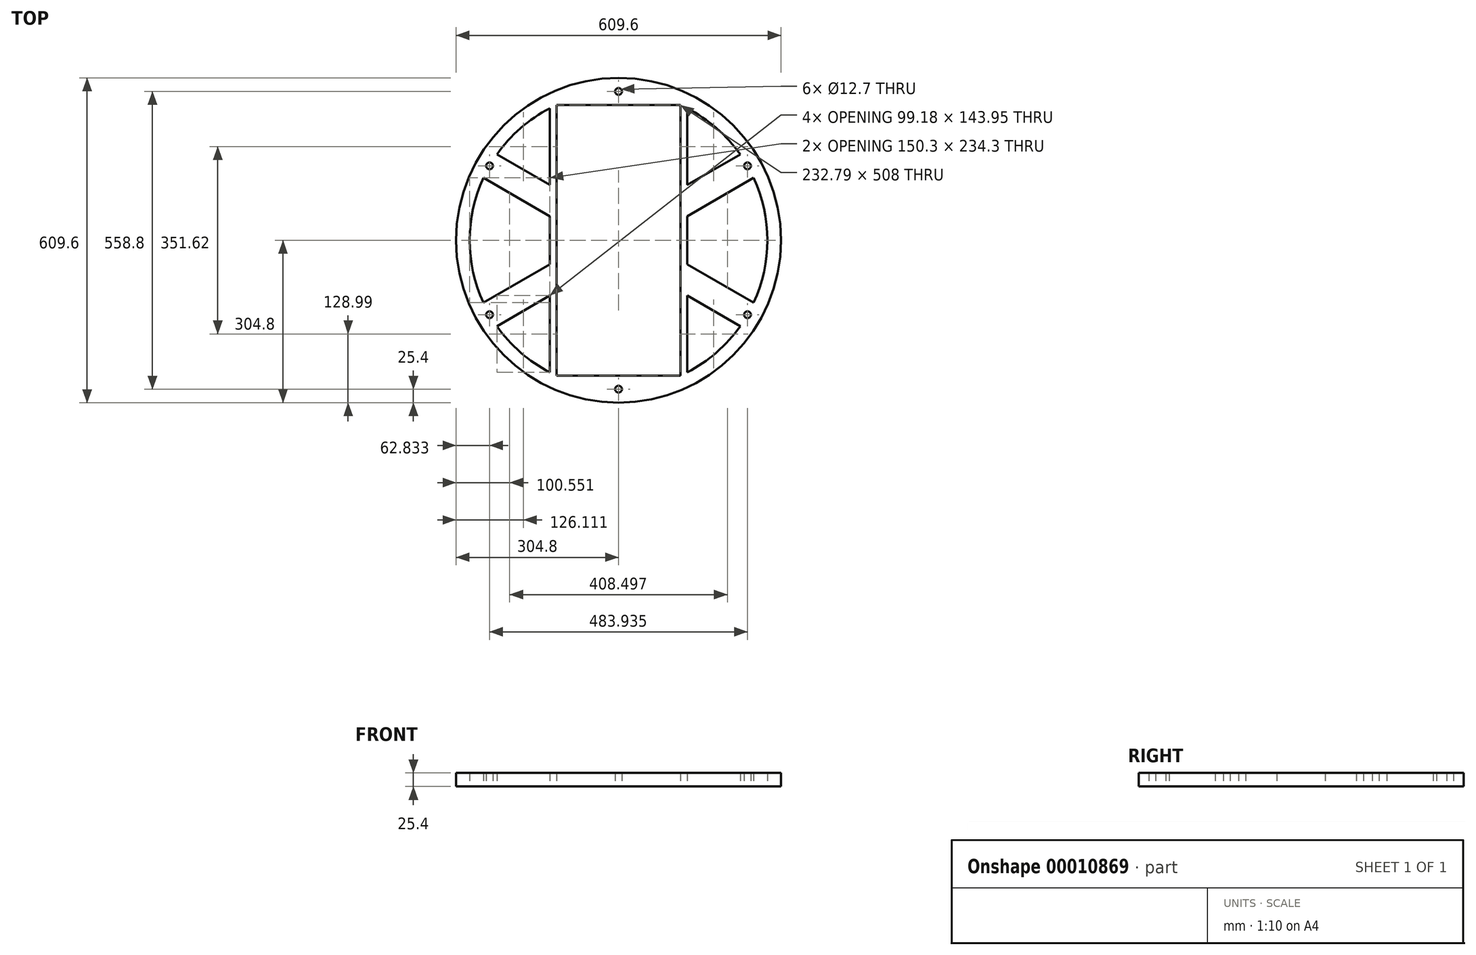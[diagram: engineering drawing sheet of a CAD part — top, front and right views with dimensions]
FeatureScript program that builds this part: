
annotation { "Feature Type Name" : "Feature", "Feature Type Description" : "" }
export const myFeature = defineFeature(function(context is Context, id is Id, definition is map)
    precondition{}
    {
        {
            var Q0;
            Q0=qCreatedBy(makeId("Top.planeOp"),FACE);
            var sketch = newSketch(context, id + "F0", { "sketchPlane" : qUnion([Q0])});
            skCircle(sketch, "E0", {"center": v(0, 0) * mm, "radius": 304.8 * mm});
            skArc(sketch, "E1.0", {"start": v(-129.1, 247.79) * mm, "mid": v(-183.87, 210.37) * mm, "end": v(-228.28, 161.1) * mm});
            skArc(sketch, "E2.1.0", {"start": v(-253.65, 117.15) * mm, "mid": v(-219.97, 127) * mm, "end": v(-228.28, 161.1) * mm});
            skArc(sketch, "E2.2.0", {"start": v(-228.28, -161.1) * mm, "mid": v(-219.97, -127) * mm, "end": v(-253.65, -117.15) * mm});
            skArc(sketch, "E2.4.0", {"start": v(253.65, -117.15) * mm, "mid": v(219.97, -127) * mm, "end": v(228.28, -161.1) * mm});
            skArc(sketch, "E2.5.0", {"start": v(228.28, 161.1) * mm, "mid": v(219.97, 127) * mm, "end": v(253.65, 117.15) * mm});
            skLineSegment(sketch, "E3.bottom", {"start": v(-116.4, 254) * mm, "end": v(116.4, 254) * mm});
            skLineSegment(sketch, "E3.top", {"start": v(-116.4, -254) * mm, "end": v(116.4, -254) * mm});
            skLineSegment(sketch, "E3.left", {"start": v(-116.4, 254) * mm, "end": v(-116.4, -254) * mm});
            skLineSegment(sketch, "E3.right", {"start": v(116.4, 254) * mm, "end": v(116.4, -254) * mm});
            skArc(sketch, "E4.trimOffspring", {"start": v(-253.65, 117.15) * mm, "mid": v(-279.4, 0) * mm, "end": v(-253.65, -117.15) * mm});
            skArc(sketch, "E5.trimOffspring", {"start": v(-228.28, -161.1) * mm, "mid": v(-183.87, -210.37) * mm, "end": v(-129.1, -247.79) * mm});
            skArc(sketch, "E6.trimOffspring", {"start": v(253.65, -117.15) * mm, "mid": v(279.4, 0) * mm, "end": v(253.65, 117.15) * mm});
            skArc(sketch, "E7.trimOffspring", {"start": v(228.28, 161.1) * mm, "mid": v(183.87, 210.37) * mm, "end": v(129.1, 247.79) * mm});
            skLineSegment(sketch, "E8.0", {"start": v(-129.1, 247.79) * mm, "end": v(-129.1, 103.83) * mm});
            skLineSegment(sketch, "E8.2", {"start": v(129.1, 247.79) * mm, "end": v(129.1, 103.83) * mm});
            skPoint(sketch, "E9.center.orphan", {"position": v(0, 279.4) * mm});
            skArc(sketch, "E10.trimOffspring", {"start": v(129.1, -247.79) * mm, "mid": v(183.87, -210.37) * mm, "end": v(228.28, -161.1) * mm});
            skLineSegment(sketch, "E11", {"start": v(-253.65, 117.15) * mm, "end": v(-129.1, 45.24) * mm});
            skLineSegment(sketch, "E12", {"start": v(-228.28, 161.1) * mm, "end": v(-129.1, 103.83) * mm});
            skLineSegment(sketch, "E13", {"start": v(-253.65, -117.15) * mm, "end": v(-129.1, -45.24) * mm});
            skLineSegment(sketch, "E14", {"start": v(253.65, 117.15) * mm, "end": v(129.1, 45.24) * mm});
            skLineSegment(sketch, "E15.trimOffspring", {"start": v(129.1, -103.83) * mm, "end": v(228.28, -161.1) * mm});
            skLineSegment(sketch, "E16.trimOffspring", {"start": v(129.1, -45.24) * mm, "end": v(253.65, -117.15) * mm});
            skLineSegment(sketch, "E17.trimOffspring", {"start": v(129.1, 103.83) * mm, "end": v(228.28, 161.1) * mm});
            skLineSegment(sketch, "E18.trimOffspring", {"start": v(-129.1, -103.83) * mm, "end": v(-228.28, -161.1) * mm});
            skLineSegment(sketch, "E19.trimOffspring", {"start": v(-129.1, -103.83) * mm, "end": v(-129.1, -247.79) * mm});
            skLineSegment(sketch, "E20.trimOffspring", {"start": v(-129.1, 45.24) * mm, "end": v(-129.1, -45.24) * mm});
            skLineSegment(sketch, "E21.trimOffspring", {"start": v(129.1, 45.24) * mm, "end": v(129.1, -45.24) * mm});
            skLineSegment(sketch, "E22.trimOffspring", {"start": v(129.1, -103.83) * mm, "end": v(129.1, -247.79) * mm});
            skCircle(sketch, "E23", {"center": v(0, 279.4) * mm, "radius": 6.35 * mm});
            skPoint(sketch, "E24.3.0", {"position": v(0, -279.4) * mm});
            skCircle(sketch, "E25.1.0", {"center": v(-241.97, 139.7) * mm, "radius": 6.35 * mm});
            skCircle(sketch, "E25.2.0", {"center": v(-241.97, -139.7) * mm, "radius": 6.35 * mm});
            skCircle(sketch, "E25.3.0", {"center": v(0, -279.4) * mm, "radius": 6.35 * mm});
            skCircle(sketch, "E25.4.0", {"center": v(241.97, -139.7) * mm, "radius": 6.35 * mm});
            skCircle(sketch, "E25.5.0", {"center": v(241.97, 139.7) * mm, "radius": 6.35 * mm});
            skSolve(sketch);
        }
        {
            var Q0;
            Q0=makeQuery(id+"F0.imprint","IMPRINT",FACE,{"disambiguationData":[TD([[makeQuery(id+"F0.imprint","IMPRINT",EDGE,{"derivedFrom":sQuery(id+"F0.wireOp",EDGE,"E0")}),1.0]])]});
            extrude(context, id + "F1", {"entities" : qUnion([Q0]), "depth" : 25.4 * mm});
        }
    });
